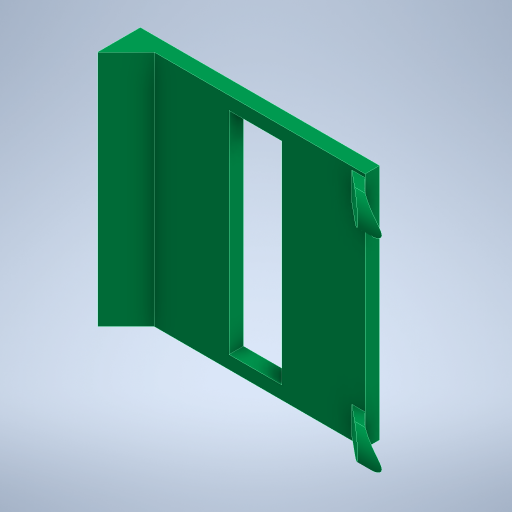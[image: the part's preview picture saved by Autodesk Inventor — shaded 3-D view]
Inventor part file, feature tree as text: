
AUTODESK INVENTOR PART (.ipt)
format: ipt  version: 2023.1 (Build 271208000, 208)  size: 486,400 bytes
history: native  units: mm
features: projected_geometry x15, extrude x8, reference x7, sketch x6, other x4, plane x2, fillet x1, mirror x1, chamfer x1
ambient origin geometry x8: Origin, YZ Plane, XZ Plane, XY Plane, X Axis, Y Axis, Z Axis, Center Point
bodies: Solid1 (feature_tree)
feature tree (45):
  extrude  "Extrusion1"  Depth=4.0mm
  sketch  "Sketch2"  dims[d2=4.0mm d3=4.0mm d4=4.0mm]
  plane  "Work Plane2"
  extrude  "Extrusion2"  Depth=4.0mm
  fillet  "Fillet1"  Radius=4.0mm
  extrude  "Extrusion3"  Depth=2.0mm
  mirror  "Mirror1"
  extrude  "Extrusion5"  Depth=2.0mm
  extrude  "Extrusion6"  Depth=1.9mm
  extrude  "Extrusion7"  Depth=10.0mm TaperAngle=0.0deg
  extrude  "Extrusion8"  Depth=10.0mm
  extrude  "Extrusion9"  Depth=10.0mm
  chamfer  "Chamfer2"  Distance=4.0mm
  sketch  "Sketch1"  dims[d0=0.15mm d1=4.0mm]
  reference  "Reference1"
  reference  "Reference2"
  reference  "Reference3"
  projected_geometry  "Projected Loop1"
  reference  "Reference4"
  reference  "Reference5"
  reference  "Reference6"
  reference  "Reference7"
  other  "Work Point1"
  plane  "Work Plane1"
  projected_geometry  "Projected Loop4"
  projected_geometry  "Projected Loop5"
  projected_geometry  "Projected Loop6"
  projected_geometry  "Projected Loop7"
  projected_geometry  "Projected Loop8"
  sketch  "Sketch5"  dims[d5=2.0mm d6=2.0mm]
  projected_geometry  "Projected Loop9"
  sketch  "Sketch6"  dims[d7=2.0mm d8=2.0mm]
  projected_geometry  "Projected Loop14"
  projected_geometry  "Projected Loop15"
  projected_geometry  "Projected Loop16"
  sketch  "Sketch7"  dims[d9=3.0mm d10=1.9mm]
  projected_geometry  "Projected Loop17"
  projected_geometry  "Projected Loop18"
  projected_geometry  "Projected Loop19"
  projected_geometry  "Projected Loop20"
  sketch  "Sketch8"  dims[d11=45.0deg d12=33.75mm d13=0.0mm d17=1.5mm d18=0.15mm d19=4.0mm d20=0.0mm d21=2.0mm d22=1.0mm d23=2.5mm d24=0.075mm d28=45.0deg d31=5.0mm d32=0.0mm d37=180.0deg d38=90.0deg d39=67.5deg d40=50.0mm d41=0.0mm d42=18.4mm d43=7.5mm d44=30.0mm d45=10.0mm d46=0.0mm d49=33.75mm d50=0.0mm d52=40.0mm d53=0.0mm d54=0.025mm d55=0.15mm d56=0.15mm d57=10.0mm d58=0.0mm d59=1.35mm d60=2.0mm d61=45.0deg]
  projected_geometry  "Projected Loop21"
  other  "Cube 1x1 V5.iam"
  other  "Cube 1x1 Bottom V5:1"
  other  "Cube 1x1 Top V5:1"
